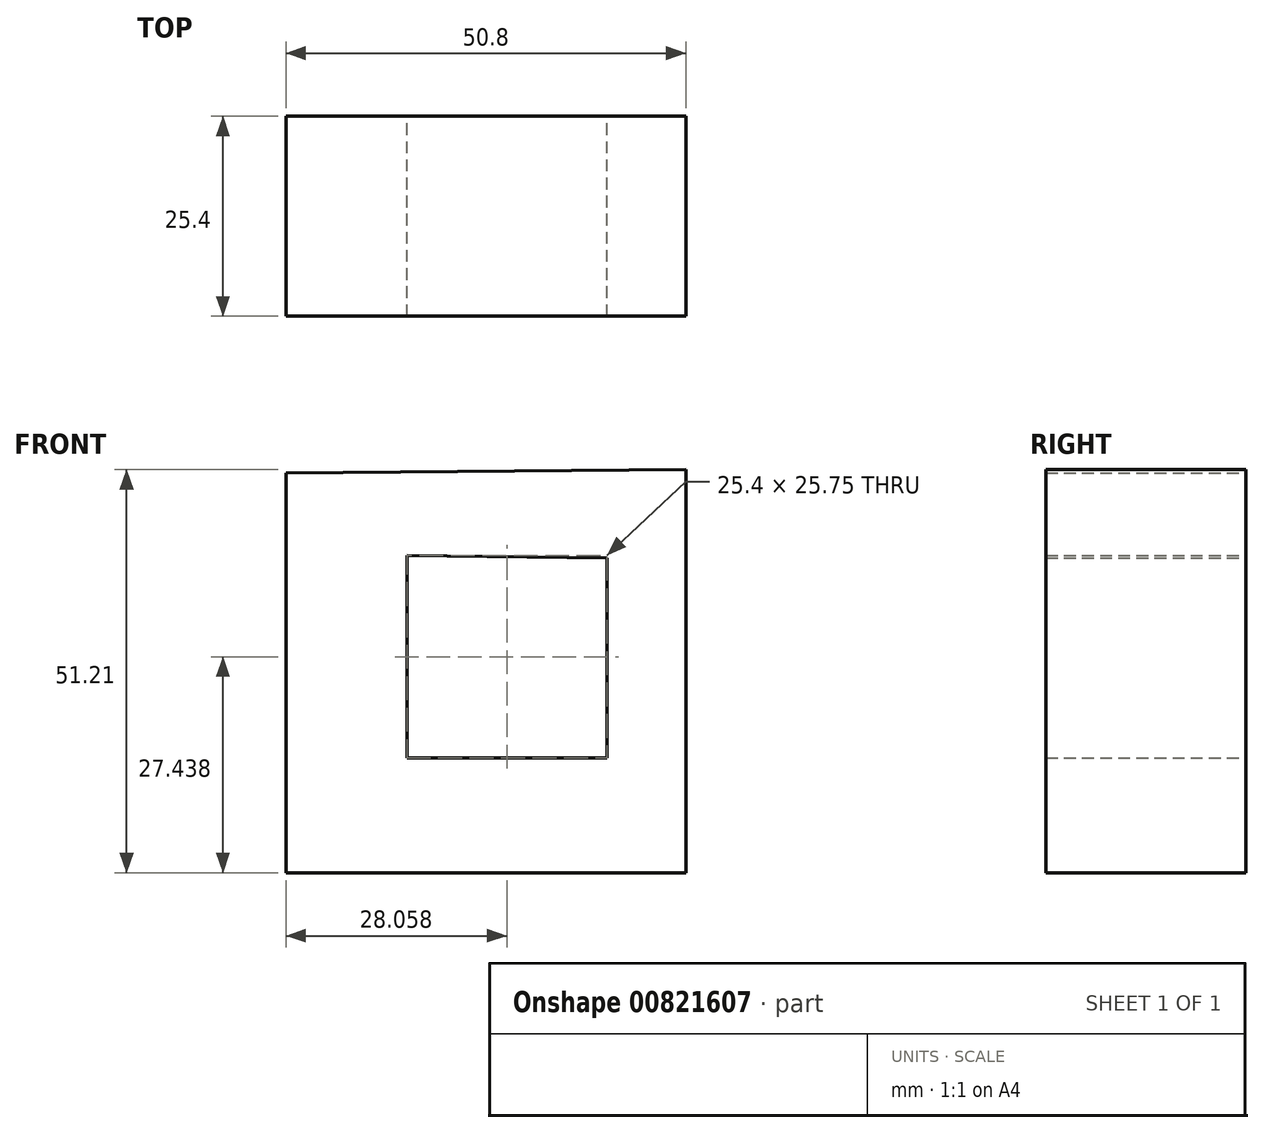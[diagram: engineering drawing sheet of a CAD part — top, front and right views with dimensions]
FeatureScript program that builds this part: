
annotation { "Feature Type Name" : "Feature", "Feature Type Description" : "" }
export const myFeature = defineFeature(function(context is Context, id is Id, definition is map)
    precondition{}
    {
        {
            var Q0;
            Q0=qCreatedBy(makeId("Front.planeOp"),FACE);
            var sketch = newSketch(context, id + "F0", { "sketchPlane" : qUnion([Q0])});
            skLineSegment(sketch, "E0", {"start": v(63, 48.5) * mm, "end": v(63, -2.3) * mm});
            skLineSegment(sketch, "E1", {"start": v(63, -2.3) * mm, "end": v(113.8, -2.3) * mm});
            skLineSegment(sketch, "E2", {"start": v(113.8, -2.3) * mm, "end": v(113.8, 48.91) * mm});
            skLineSegment(sketch, "E3", {"start": v(113.8, 48.91) * mm, "end": v(63, 48.5) * mm});
            skLineSegment(sketch, "E4", {"start": v(78.37, 38.01) * mm, "end": v(78.37, 12.26) * mm});
            skLineSegment(sketch, "E5", {"start": v(78.37, 12.26) * mm, "end": v(103.77, 12.26) * mm});
            skLineSegment(sketch, "E6", {"start": v(103.77, 12.26) * mm, "end": v(103.77, 37.66) * mm});
            skLineSegment(sketch, "E7", {"start": v(103.77, 37.66) * mm, "end": v(78.37, 38.01) * mm});
            skSolve(sketch);
        }
        {
            var Q0;
            Q0=makeQuery(id+"F0.imprint","IMPRINT",FACE,{"disambiguationData":[TD([[makeQuery(id+"F0.imprint","IMPRINT",EDGE,{"derivedFrom":sQuery(id+"F0.wireOp",EDGE,"E0")}),1.0]])]});
            extrude(context, id + "F1", {"entities" : qUnion([Q0]), "depth" : 25.4 * mm, "offsetDistance" : 25.4 * mm});
        }
    });
